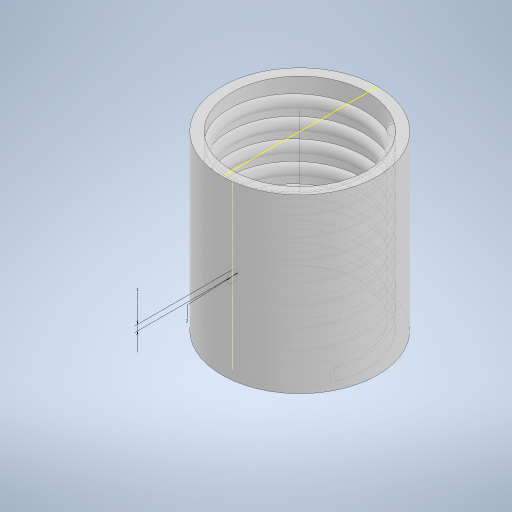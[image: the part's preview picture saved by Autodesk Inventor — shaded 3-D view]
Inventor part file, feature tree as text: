
AUTODESK INVENTOR PART (.ipt)
format: ipt  version: 2024.1 (Build 281209000, 209)  size: 642,048 bytes
history: native  units: mm
features: sketch x4, helix x3, fillet x3, projected_geometry x3, extrude x2
ambient origin geometry x8: Origin, YZ Plane, XZ Plane, XY Plane, X Axis, Y Axis, Z Axis, Center Point
bodies: Solid1 (feature_tree), Solid2 (feature_tree)
feature tree (15):
  extrude  "Extrusion1"  Depth=18.0mm
  helix  "Coil1"  [1 undecoded]
  fillet  "Fillet1"  Radius=2.15mm
  extrude  "Extrusion2"  Depth=1.0mm
  sketch  "Sketch4"  dims[d20=1.0mm d21=3.4mm d22=13.0mm d23=50.0mm d24=0.0mm d25=90.0deg d26=90.0deg d27=0.0mm d28=0.0mm d29=3.4mm d30=15.0mm d31=50.0mm d32=0.0mm d33=90.0deg d34=90.0deg d35=0.0mm d36=0.0mm d37=0.9mm d38=0.9mm]
  helix  "Coil2"  [1 undecoded]
  helix  "Coil3"  [1 undecoded]
  fillet  "Fillet2"  Radius=30.0mm
  fillet  "Fillet3"  Radius=2.0mm
  sketch  "Sketch1"  dims[d0=21.12mm d1=18.0mm d2=14.0mm d3=0.0mm d4=2.15mm]
  sketch  "Sketch2"  dims[d5=2.8mm]
  projected_geometry  "Projected Loop1"
  sketch  "Sketch3"  dims[d6=3.4mm d7=10.0mm d8=50.0mm d9=0.0mm d10=90.0deg d11=90.0deg d12=0.0mm d13=0.0mm d14=1.0mm d15=3.0mm d16=1.23mm d17=30.0mm d18=0.0mm d19=2.0mm]
  projected_geometry  "Projected Loop2"
  projected_geometry  "Projected Loop3"
note: 3 required parameter values undecoded (feature->parameter linkage not recoverable at this tier; creation-order binding heuristic only, values carry confidence <= 0.55)
